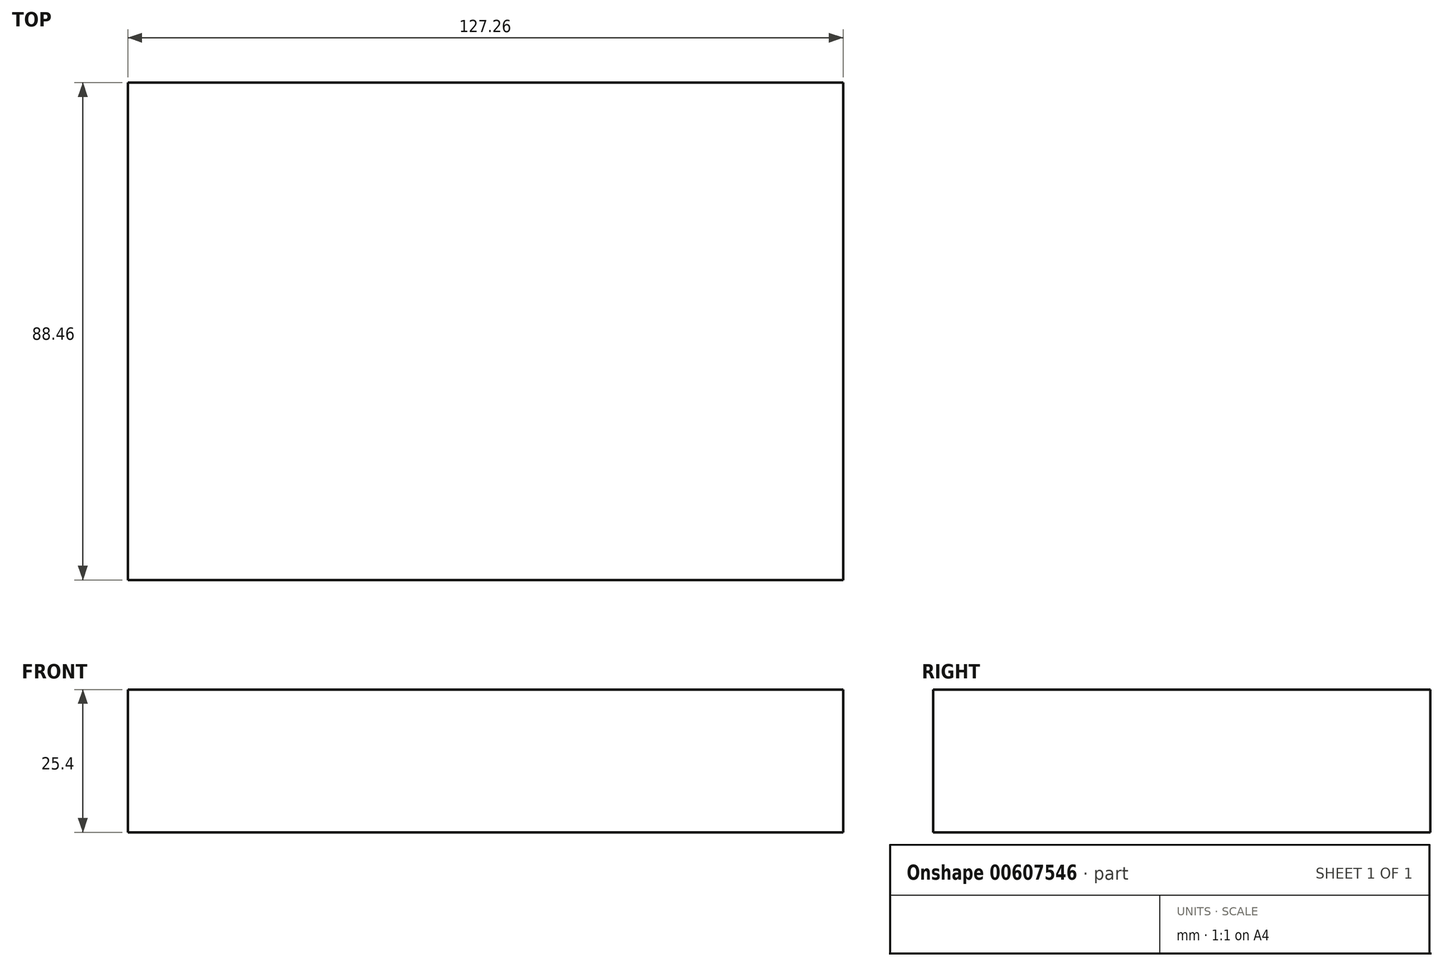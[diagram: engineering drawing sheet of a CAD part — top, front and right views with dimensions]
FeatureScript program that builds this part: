
annotation { "Feature Type Name" : "Feature", "Feature Type Description" : "" }
export const myFeature = defineFeature(function(context is Context, id is Id, definition is map)
    precondition{}
    {
        {
            var Q0;
            Q0=qCreatedBy(makeId("Top.planeOp"),FACE);
            var sketch = newSketch(context, id + "F0", { "sketchPlane" : qUnion([Q0])});
            skLineSegment(sketch, "E0.bottom", {"start": v(63.63, -44.23) * mm, "end": v(-63.63, -44.23) * mm});
            skLineSegment(sketch, "E0.top", {"start": v(63.63, 44.23) * mm, "end": v(-63.63, 44.23) * mm});
            skLineSegment(sketch, "E0.left", {"start": v(63.63, -44.23) * mm, "end": v(63.63, 44.23) * mm});
            skLineSegment(sketch, "E0.right", {"start": v(-63.63, -44.23) * mm, "end": v(-63.63, 44.23) * mm});
            skPoint(sketch, "E0.middle", {"position": v(0, 0) * mm});
            skSolve(sketch);
        }
        {
            var Q0;
            Q0 = qSketchRegion(id + "F0", true);
            extrude(context, id + "F1", {"entities" : qUnion([Q0]), "depth" : 25.4 * mm, "offsetDistance" : 25.4 * mm});
        }
    });
